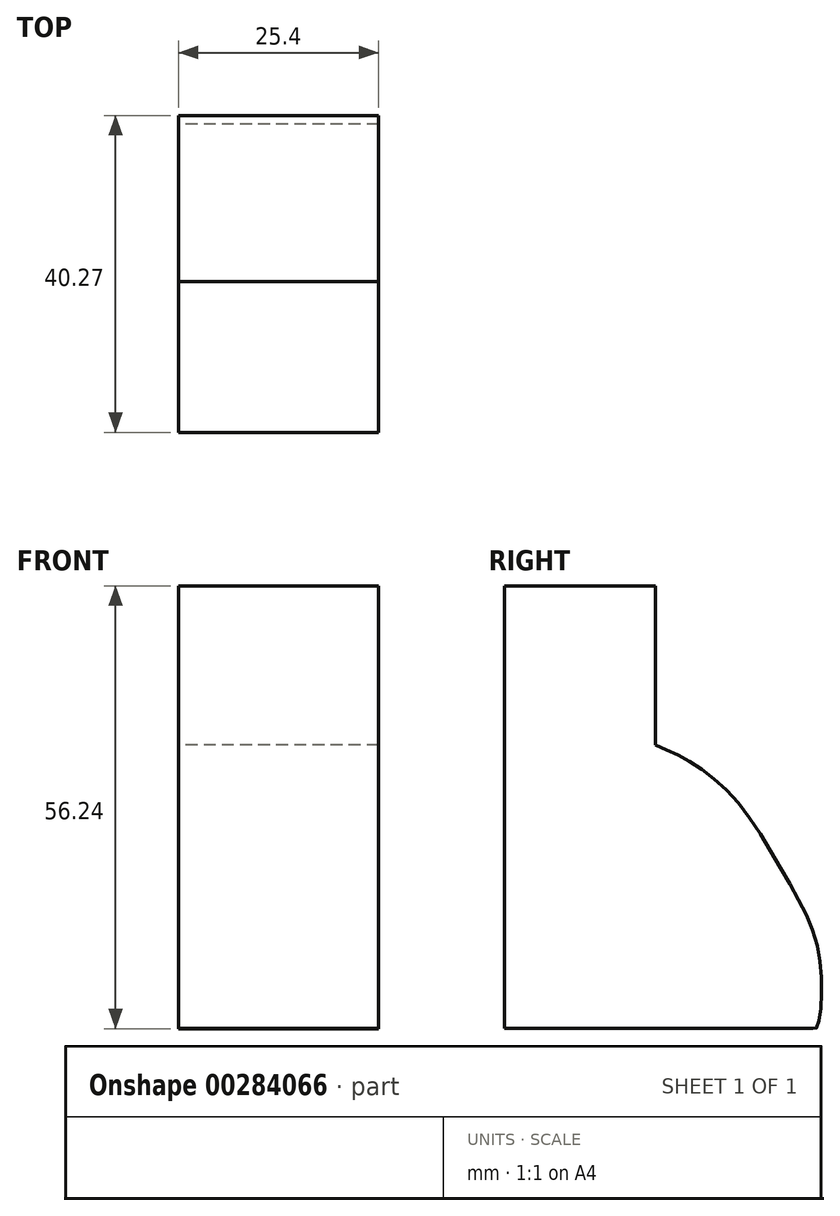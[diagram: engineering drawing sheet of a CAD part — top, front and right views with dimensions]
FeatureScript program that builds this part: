
annotation { "Feature Type Name" : "Feature", "Feature Type Description" : "" }
export const myFeature = defineFeature(function(context is Context, id is Id, definition is map)
    precondition{}
    {
        {
            var Q0;
            Q0=qCreatedBy(makeId("Right.planeOp"),FACE);
            var sketch = newSketch(context, id + "F0", { "sketchPlane" : qUnion([Q0])});
            skLineSegment(sketch, "E0", {"start": v(-56.07, 56.18) * mm, "end": v(-36.92, 56.18) * mm});
            skLineSegment(sketch, "E1", {"start": v(-36.92, 56.18) * mm, "end": v(-36.92, 35.96) * mm});
            skFitSpline(sketch, "E2", {"points": [v(-36.92, 35.96) * mm, v(-32.45, 33.83) * mm, v(-26.5, 28.73) * mm, v(-20.32, 19.15) * mm, v(-16.5, 11.06) * mm, v(-15.85, 3.4) * mm, v(-16.5, 0) * mm, v(-16.92, 0) * mm], "startDerivative": vector(32.82, -13.55) * mm, "endDerivative": vector(-11.44, 3.8) * mm});
            skLineSegment(sketch, "E3", {"start": v(-56.07, 56.18) * mm, "end": v(-56.07, 0) * mm});
            skLineSegment(sketch, "E4", {"start": v(-56.07, 0) * mm, "end": v(-16.92, 0) * mm});
            skSolve(sketch);
        }
        {
            var Q0;
            Q0 = qSketchRegion(id + "F0", true);
            extrude(context, id + "F1", {"entities" : qUnion([Q0]), "depth" : 25.4 * mm});
        }
    });
